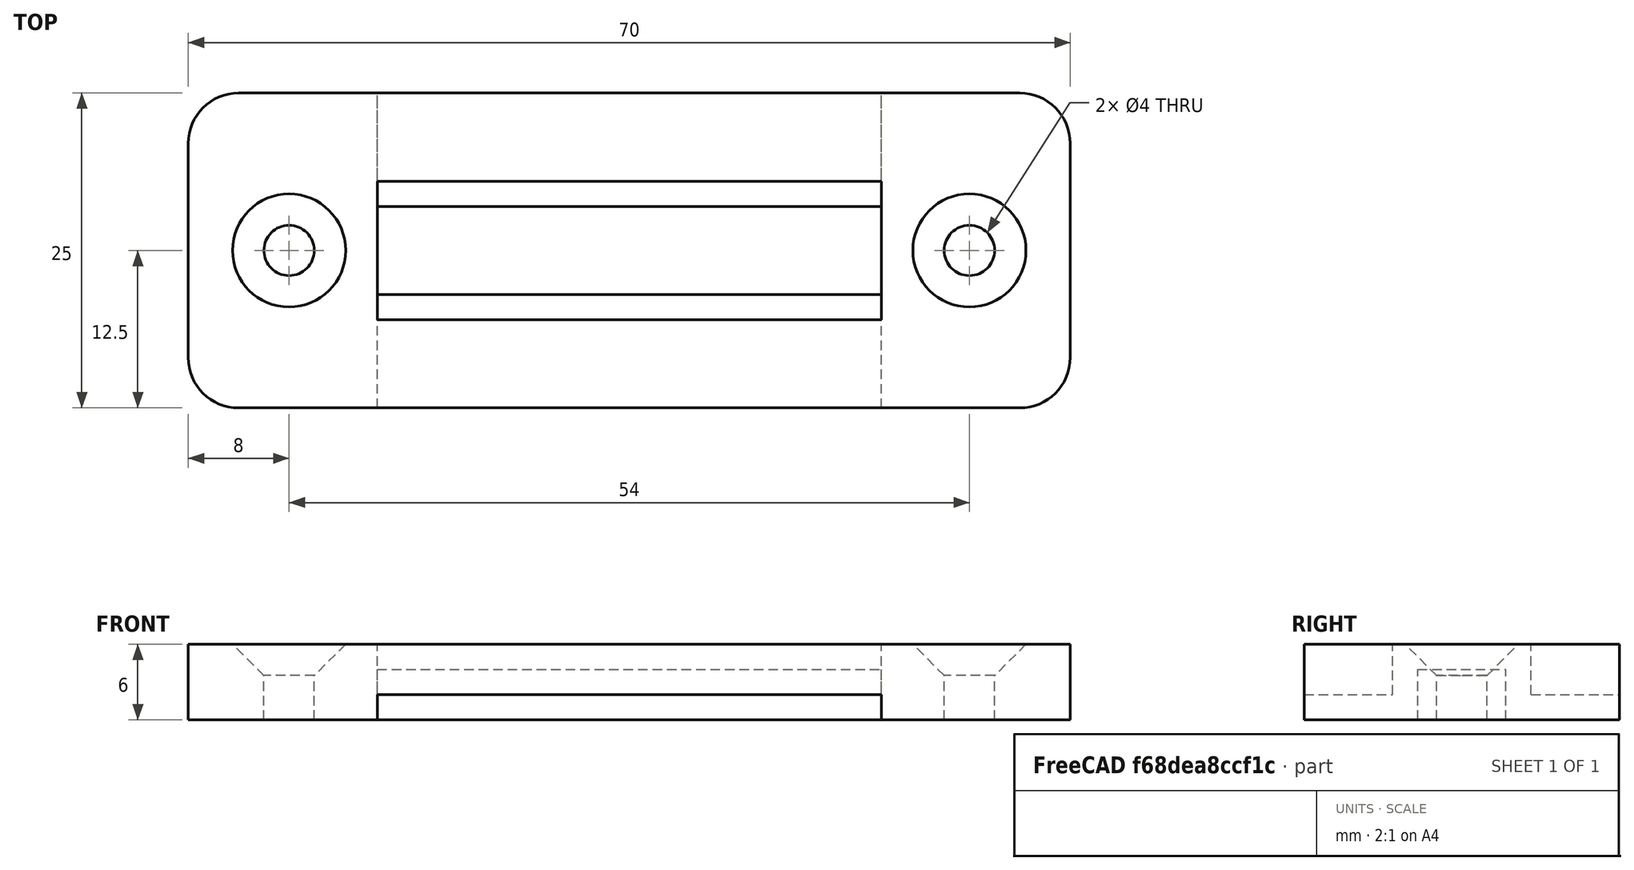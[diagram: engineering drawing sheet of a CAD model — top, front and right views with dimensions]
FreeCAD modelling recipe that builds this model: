
FCSTD DOCUMENT  (FreeCAD 0.18R4 (GitTag))
Label: Buckle
License: All rights reserved
LicenseURL: http://en.wikipedia.org/wiki/All_rights_reserved
objects: Part::Box×4, Part::Cut×3, Part::Cylinder×2, Part::MultiFuse×2, Part::Chamfer×1, Part::Fillet×1
note: 13 computed .brp shape members not serialized (recipe doc carries the construction recipe); baked Part::Feature solids carry a one-line shape summary decoded from their .brp

FEATURE [Part::Box] Box  label="Base001"
  AttacherType = Attacher::AttachEngine3D
  Height = 6
  Length = 70
  Placement = pos=(-35,-20,0) rot=(0,0,1;0rad)
  Width = 25
FEATURE [Part::Box] Box001  label="Cube"
  AttacherType = Attacher::AttachEngine3D
  Height = 2
  Length = 40
  Placement = pos=(-20,-20,0) rot=(0,0,1;0rad)
  Width = 25
FEATURE [Part::Box] Box003  label="hole 2"
  AttacherType = Attacher::AttachEngine3D
  Height = 4
  Length = 40
  Placement = pos=(-20,-11,0) rot=(0,0,1;0rad)
  Width = 7
FEATURE [Part::Cylinder] Cylinder001  label="ScrewHole002"
  Angle = 360
  AttacherType = Attacher::AttachEngine3D
  Height = 10
  Placement = pos=(-27,-7.5,0) rot=(0,0,1;0rad)
  Radius = 2
FEATURE [Part::Cylinder] Cylinder003  label="ScrewHole004"
  Angle = 360
  AttacherType = Attacher::AttachEngine3D
  Height = 10
  Placement = pos=(27,-7.5,0) rot=(0,0,1;0rad)
  Radius = 2
FEATURE [Part::MultiFuse] Fusion001  label="ScrewHoles"
  Refine = true
  Shapes = -> [Cylinder003,Cylinder001]
FEATURE [Part::Cut] Cut  label="Base002"
  Base = -> Box
  Refine = true
  Tool = -> Box001
FEATURE [Part::Box] Box006  label="Cube001"
  AttacherType = Attacher::AttachEngine3D
  Height = 10
  Length = 40
  Placement = pos=(-20,-13,0) rot=(0,0,1;0rad)
  Width = 11
FEATURE [Part::Cut] Cut001
  Base = -> Cut
  Refine = true
  Tool = -> Box006
FEATURE [Part::Cut] Cut002
  Base = -> Cut001
  Refine = true
  Tool = -> Fusion001
FEATURE [Part::Chamfer] Chamfer
  Base = -> Cut002
  Edges = 2 edges r=2.49: [Edge14,Edge19]
FEATURE [Part::Fillet] Fillet
  Base = -> Chamfer
  Edges = 4 edges r=4: [Edge13,Edge14,Edge21,Edge27]
FEATURE [Part::MultiFuse] Fusion
  Refine = true
  Shapes = -> [Box003,Fillet]
